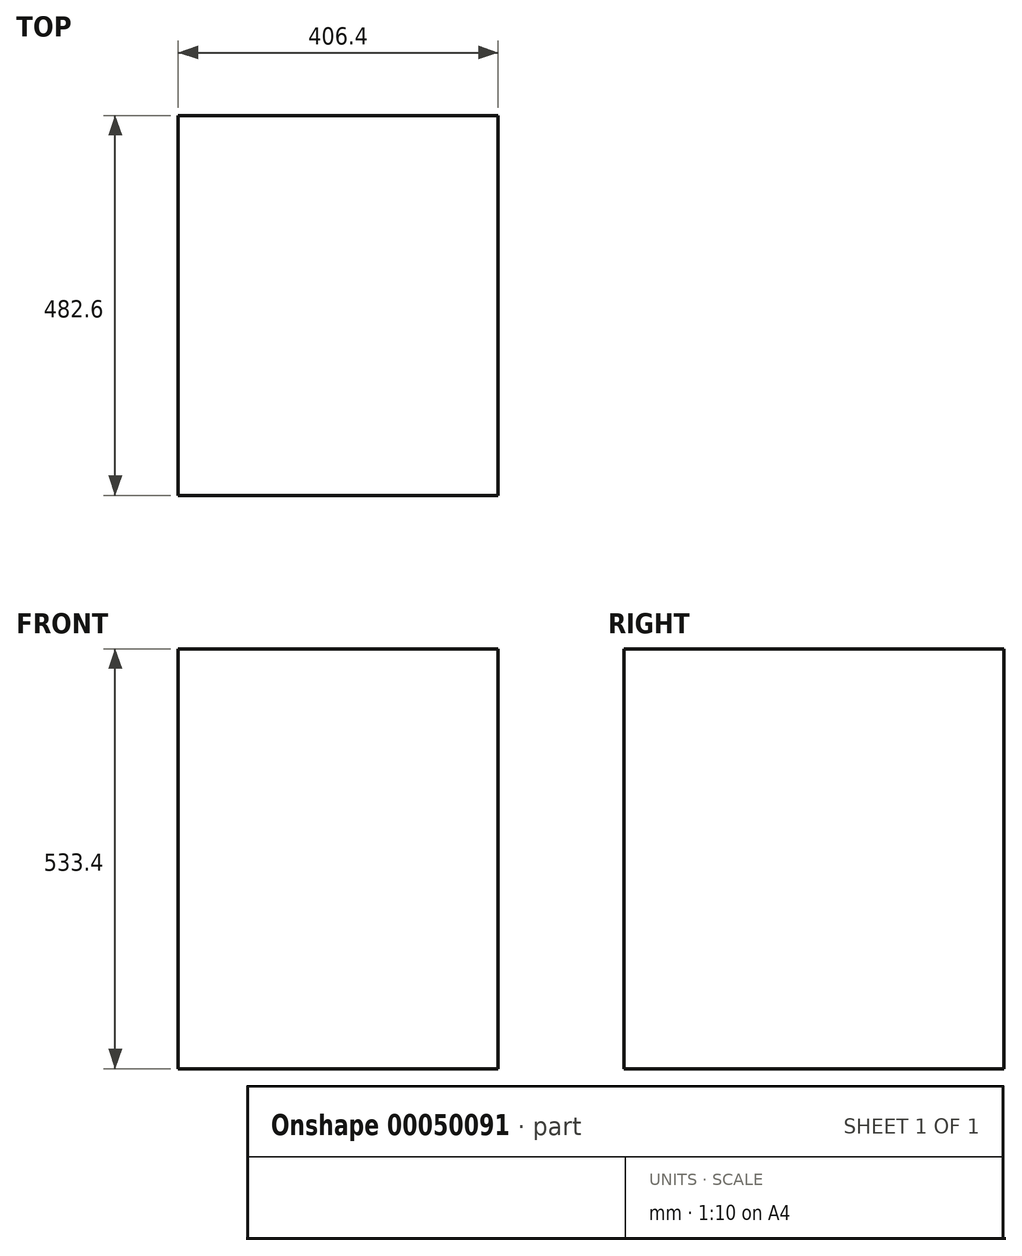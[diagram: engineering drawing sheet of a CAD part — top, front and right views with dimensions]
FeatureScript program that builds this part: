
annotation { "Feature Type Name" : "Feature", "Feature Type Description" : "" }
export const myFeature = defineFeature(function(context is Context, id is Id, definition is map)
    precondition{}
    {
        {
            var Q0;
            Q0=qCreatedBy(makeId("Top.planeOp"),FACE);
            var sketch = newSketch(context, id + "F0", { "sketchPlane" : qUnion([Q0])});
            skLineSegment(sketch, "E0.bottom", {"start": v(-203.2, 241.3) * mm, "end": v(203.2, 241.3) * mm});
            skLineSegment(sketch, "E0.top", {"start": v(-203.2, -241.3) * mm, "end": v(203.2, -241.3) * mm});
            skLineSegment(sketch, "E0.left", {"start": v(-203.2, 241.3) * mm, "end": v(-203.2, -241.3) * mm});
            skLineSegment(sketch, "E0.right", {"start": v(203.2, 241.3) * mm, "end": v(203.2, -241.3) * mm});
            skSolve(sketch);
        }
        {
            var Q0;
            Q0 = qSketchRegion(id + "F0", true);
            extrude(context, id + "F1", {"entities" : qUnion([Q0]), "depth" : 533.4 * mm});
        }
    });
